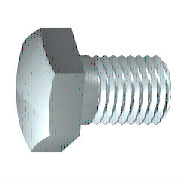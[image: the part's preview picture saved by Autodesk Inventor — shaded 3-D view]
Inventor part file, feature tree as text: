
AUTODESK INVENTOR PART (.ipt)
format: ipt  version: 2023.2 (Build 272271030, 271C)  size: 188,928 bytes
history: native  units: mm (DEFAULTED — no unit token found)
features: sketch x3, extrude x1, chamfer x1, plane x1
ambient origin geometry x7: Origin, YZ Plane, XZ Plane, X Axis, Y Axis, Z Axis, Center Point
bodies: Solid1 (feature_tree), Body (feature_tree)
feature tree (6):
  extrude  "Head"  Depth=94.7mm
  chamfer  "Chamfer1"  Distance=6.9mm
  plane  "Work Plane1"
  sketch  "Sketch1"  dims[d0=100.0mm d1=94.7mm]
  sketch  "Sketch2"  dims[d2=12.0mm]
  sketch  "Sketch4"  dims[d12=90.0deg d3=6.9mm d4=0.0mm d5=30.0deg d21=90.0deg d6=1.073538mm d7=1.073638mm d8=0.0mm d9=0.6001mm d10=16.63mm d11=18.0mm d13=1.073638mm d14=12.0mm d15=94.7mm d16=0.0mm d19=18.0mm d55=45.0deg d57=0.0mm d58=0.0mm]
